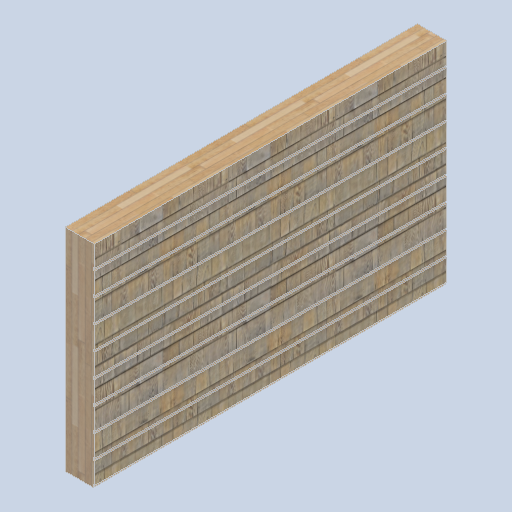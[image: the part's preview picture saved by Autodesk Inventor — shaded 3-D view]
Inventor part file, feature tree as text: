
AUTODESK INVENTOR PART (.ipt)
format: ipt  version: 2024.2 (Build 282272000, 272)  size: 368,128 bytes
history: native  units: in
note: dims shown in document units (in); Inventor stores cm internally (conversion verified against a paired STEP export)
features: other x3, sketch x2
ambient origin geometry x8: Origin, YZ Plane, XZ Plane, XY Plane, X Axis, Y Axis, Z Axis, Center Point
bodies: Solid1 (feature_tree)
feature tree (5):
  other  "side_wall_block_02.ipt"
  other  "Solid1::side_wall_block_02.ipt"
  other  "TaggingFeature1"
  sketch  "Sketch1"  dims[d0=0.3937in]
  sketch  "Sketch2"
